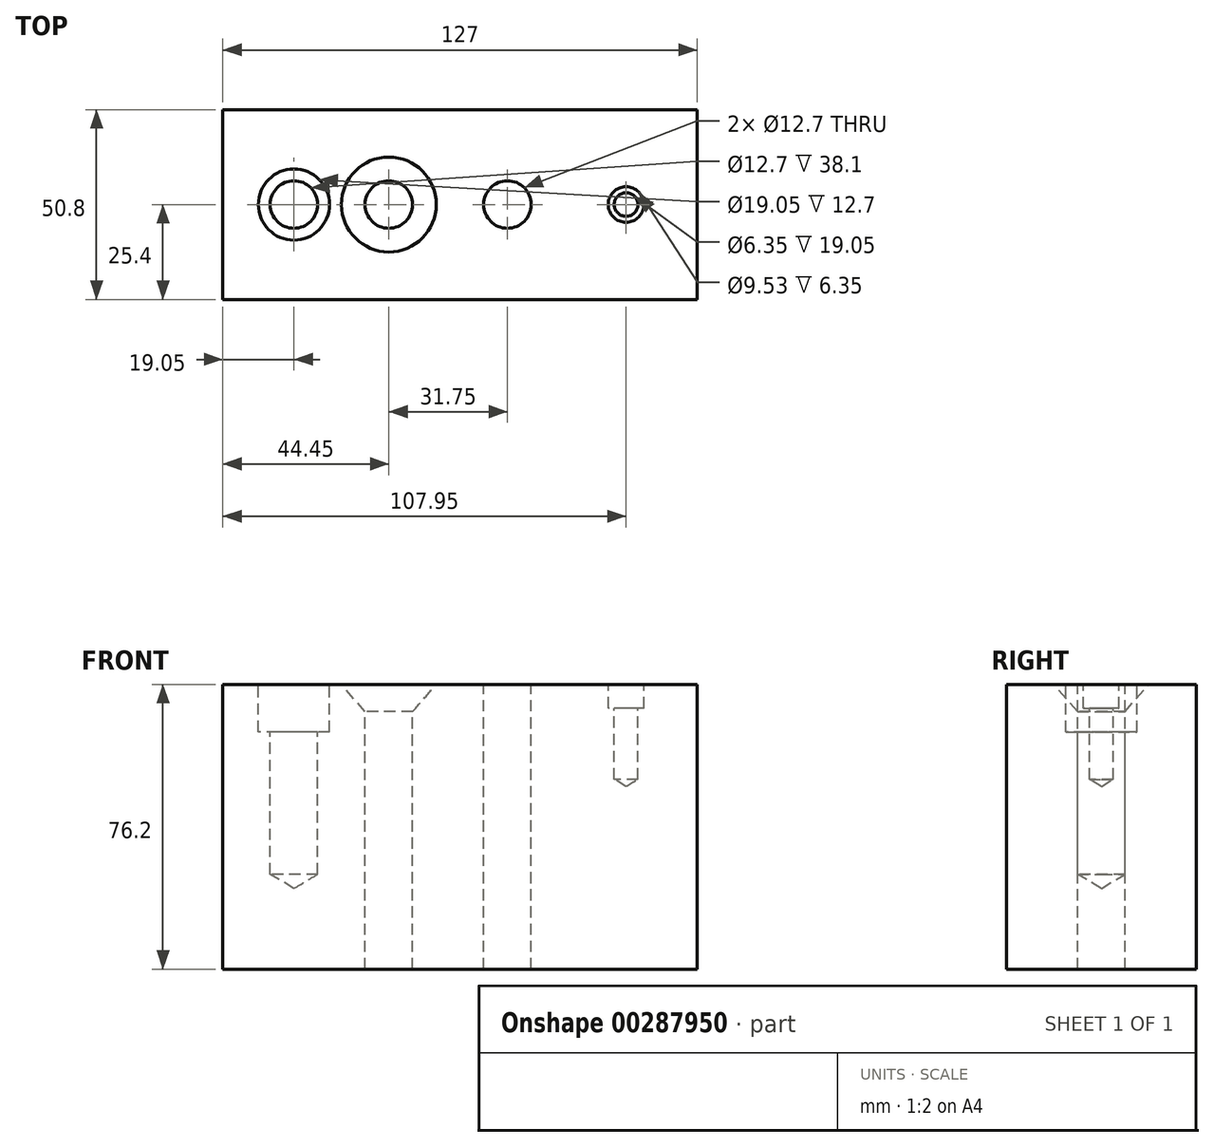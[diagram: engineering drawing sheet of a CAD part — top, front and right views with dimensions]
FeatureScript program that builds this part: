
annotation { "Feature Type Name" : "Feature", "Feature Type Description" : "" }
export const myFeature = defineFeature(function(context is Context, id is Id, definition is map)
    precondition{}
    {
        {
            var Q0;
            Q0=qCreatedBy(makeId("Top.planeOp"),FACE);
            var sketch = newSketch(context, id + "F0", { "sketchPlane" : qUnion([Q0])});
            skLineSegment(sketch, "E0.bottom", {"start": v(-60.15, 47.5) * mm, "end": v(66.85, 47.5) * mm});
            skLineSegment(sketch, "E0.top", {"start": v(-60.15, -3.3) * mm, "end": v(66.85, -3.3) * mm});
            skLineSegment(sketch, "E0.left", {"start": v(-60.15, 47.5) * mm, "end": v(-60.15, -3.3) * mm});
            skLineSegment(sketch, "E0.right", {"start": v(66.85, 47.5) * mm, "end": v(66.85, -3.3) * mm});
            skSolve(sketch);
        }
        {
            var Q0;
            Q0=makeQuery(id+"F0.imprint","IMPRINT",FACE,{"disambiguationData":[TD([[makeQuery(id+"F0.imprint","IMPRINT",EDGE,{"derivedFrom":sQuery(id+"F0.wireOp",EDGE,"E0.bottom")}),-1.0]])]});
            extrude(context, id + "F1", {"entities" : qUnion([Q0]), "depth" : 76.2 * mm, "offsetDistance" : 25.4 * mm});
        }
        {
            var Q0;
            Q0=makeQuery(id+"F1.opExtrude","CAP_FACE",FACE,{"disambiguationData":[OSD([sQuery(id+"F0.wireOp",EDGE,"E0.bottom"),sQuery(id+"F0.wireOp",EDGE,"E0.top"),sQuery(id+"F0.wireOp",EDGE,"E0.left"),sQuery(id+"F0.wireOp",EDGE,"E0.right")])],"isStart":false});
            var sketch = newSketch(context, id + "F2", { "sketchPlane" : qUnion([Q0])});
            skLineSegment(sketch, "E1", {"start": v(-62.02, 22.1) * mm, "end": v(90.6, 22.1) * mm, "construction": true});
            skLineSegment(sketch, "E2", {"start": v(-41.1, 55.65) * mm, "end": v(-41.1, -11.42) * mm, "construction": true});
            skLineSegment(sketch, "E3", {"start": v(-15.7, 54.76) * mm, "end": v(-15.7, -19) * mm, "construction": true});
            skLineSegment(sketch, "E4", {"start": v(16.05, 53.7) * mm, "end": v(16.05, -18.64) * mm, "construction": true});
            skLineSegment(sketch, "E5", {"start": v(47.8, 53) * mm, "end": v(47.8, -13) * mm, "construction": true});
            skCircle(sketch, "E6", {"center": v(16.05, 22.1) * mm, "radius": 6.35 * mm});
            skCircle(sketch, "E7", {"center": v(47.8, 22.1) * mm, "radius": 3.18 * mm});
            skCircle(sketch, "E8", {"center": v(47.8, 22.1) * mm, "radius": 4.76 * mm});
            skCircle(sketch, "E9", {"center": v(-15.7, 22.1) * mm, "radius": 12.7 * mm});
            skCircle(sketch, "E10", {"center": v(-15.7, 22.1) * mm, "radius": 6.35 * mm});
            skCircle(sketch, "E11", {"center": v(-41.1, 22.1) * mm, "radius": 9.53 * mm});
            skCircle(sketch, "E12", {"center": v(-41.1, 22.1) * mm, "radius": 6.35 * mm});
            skSolve(sketch);
        }
        {
            var Q0;
            Q0=makeQuery(id+"F2.imprint","IMPRINT",FACE,{"disambiguationData":[TD([[makeQuery(id+"F2.imprint","IMPRINT",EDGE,{"derivedFrom":sQuery(id+"F2.wireOp",EDGE,"E6")}),1.0]])]});
            extrude(context, id + "F3", {"entities" : qUnion([Q0]), "operationType" : NewBodyOperationType.REMOVE, "endBound" : BoundingType.THROUGH_ALL, "oppositeDirection" : true, "depth" : 25.4 * mm, "offsetDistance" : 25.4 * mm});
        }
        {
            var Q0;
            Q0=sQuery(id+"F2.wireOp",VERTEX,"E10.center");
            var Q1;
            Q1=makeQuery(id+"F1.opExtrude","SWEPT_BODY",BODY,{"disambiguationData":[OSD([sQuery(id+"F0.wireOp",EDGE,"E0.bottom"),sQuery(id+"F0.wireOp",EDGE,"E0.top"),sQuery(id+"F0.wireOp",EDGE,"E0.left"),sQuery(id+"F0.wireOp",EDGE,"E0.right")])]});
            hole(context, id + "F4", {"style" : HoleStyle.C_SINK, "endStyle" : HoleEndStyle.THROUGH, "holeDiameter" : 12.7 * mm, "cSinkDiameter" : 25.4 * mm, "cSinkAngle" : 82 * degree, "isTappedThrough" : true, "tappedDepth" : 12.7 * mm, "tapClearance" : 3, "locations" : qUnion([Q0]), "scope" : qUnion([Q1])});
        }
        {
            var Q0;
            Q0=sQuery(id+"F2.wireOp",VERTEX,"E12.center");
            var Q1;
            Q1=makeQuery(id+"F1.opExtrude","SWEPT_BODY",BODY,{"disambiguationData":[OSD([sQuery(id+"F0.wireOp",EDGE,"E0.bottom"),sQuery(id+"F0.wireOp",EDGE,"E0.top"),sQuery(id+"F0.wireOp",EDGE,"E0.left"),sQuery(id+"F0.wireOp",EDGE,"E0.right")])]});
            hole(context, id + "F5", {"style" : HoleStyle.C_BORE, "endStyle" : HoleEndStyle.BLIND, "holeDiameter" : 12.7 * mm, "cBoreDiameter" : 19.05 * mm, "cBoreDepth" : 12.7 * mm, "holeDepth" : 50.8 * mm, "isTappedThrough" : true, "tappedDepth" : 12.7 * mm, "tapClearance" : 3, "locations" : qUnion([Q0]), "scope" : qUnion([Q1])});
        }
        {
            var Q0;
            Q0=sQuery(id+"F2.wireOp",VERTEX,"E8.center");
            var Q1;
            Q1=makeQuery(id+"F1.opExtrude","SWEPT_BODY",BODY,{"disambiguationData":[OSD([sQuery(id+"F0.wireOp",EDGE,"E0.bottom"),sQuery(id+"F0.wireOp",EDGE,"E0.top"),sQuery(id+"F0.wireOp",EDGE,"E0.left"),sQuery(id+"F0.wireOp",EDGE,"E0.right")])]});
            hole(context, id + "F6", {"style" : HoleStyle.C_BORE, "endStyle" : HoleEndStyle.BLIND, "holeDiameter" : 6.35 * mm, "cBoreDiameter" : 9.52 * mm, "cBoreDepth" : 6.35 * mm, "holeDepth" : 25.4 * mm, "isTappedThrough" : true, "tappedDepth" : 12.7 * mm, "tapClearance" : 3, "locations" : qUnion([Q0]), "scope" : qUnion([Q1])});
        }
    });
